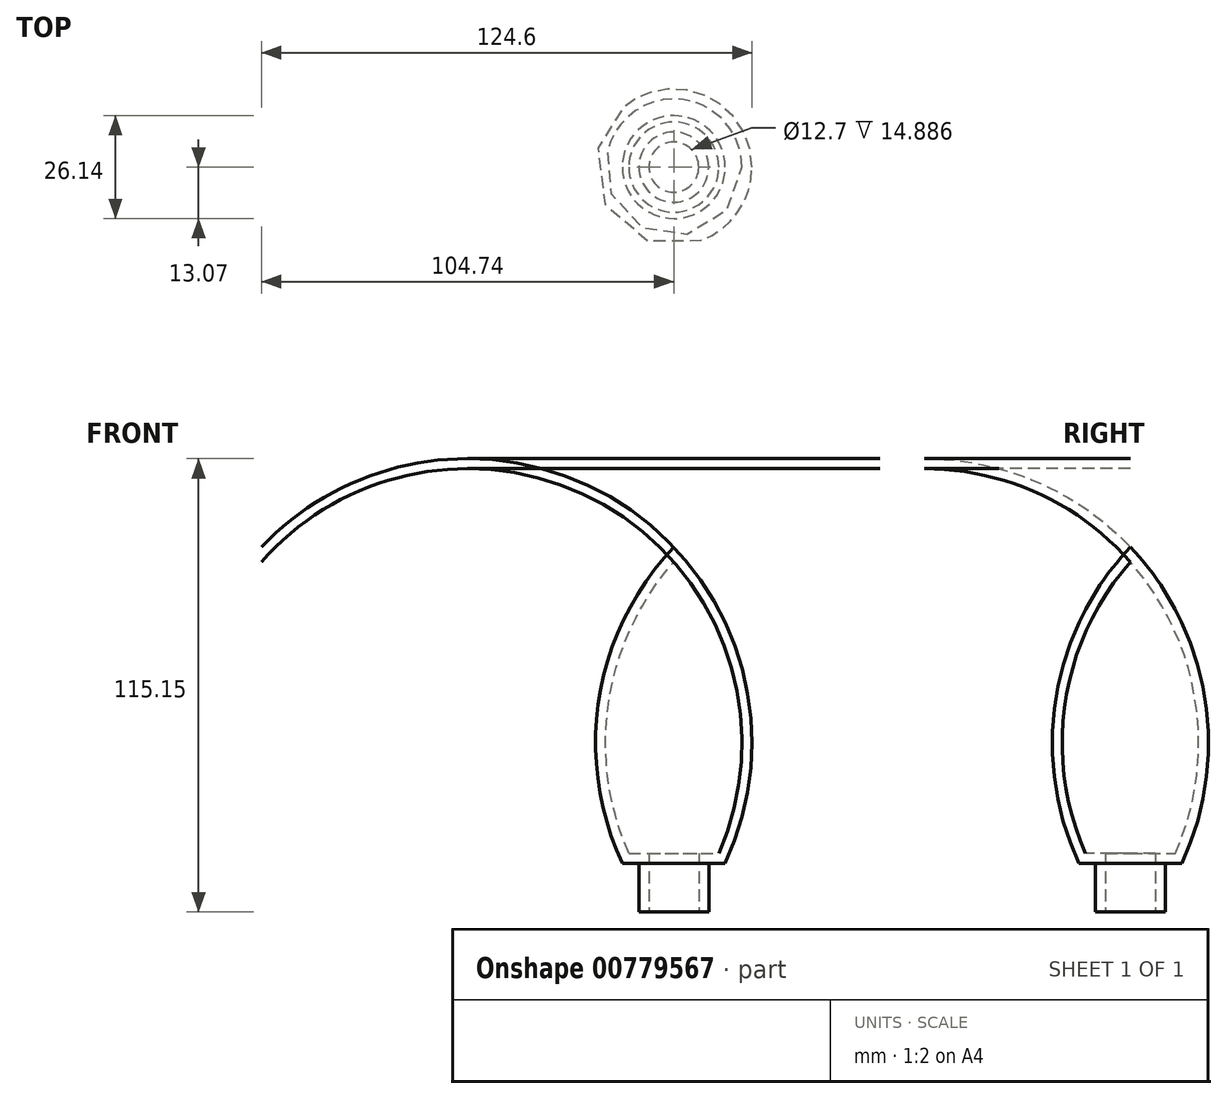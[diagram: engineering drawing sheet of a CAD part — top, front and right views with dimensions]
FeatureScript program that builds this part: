
annotation { "Feature Type Name" : "Feature", "Feature Type Description" : "" }
export const myFeature = defineFeature(function(context is Context, id is Id, definition is map)
    precondition{}
    {
        {
            var Q0;
            Q0=qCreatedBy(makeId("Front.planeOp"),FACE);
            var sketch = newSketch(context, id + "F0", { "sketchPlane" : qUnion([Q0])});
            skLineSegment(sketch, "E0", {"start": v(0, 0) * mm, "end": v(0, 88.9) * mm});
            skLineSegment(sketch, "E1", {"start": v(6.35, 0) * mm, "end": v(6.35, 14.89) * mm});
            skLineSegment(sketch, "E2", {"start": v(6.35, 14.89) * mm, "end": v(11.43, 14.89) * mm});
            skArc(sketch, "E3", {"start": v(11.43, 14.89) * mm, "mid": v(16.5, 53.56) * mm, "end": v(0, 88.9) * mm});
            skArc(sketch, "E4.0", {"start": v(13.07, 12.35) * mm, "mid": v(18.28, 57.96) * mm, "end": v(-5.05, 97.5) * mm});
            skLineSegment(sketch, "E4.1", {"start": v(8.9, 12.35) * mm, "end": v(13.07, 12.35) * mm});
            skLineSegment(sketch, "E4.2", {"start": v(8.9, 0) * mm, "end": v(8.9, 12.35) * mm});
            skLineSegment(sketch, "E5", {"start": v(6.35, 0) * mm, "end": v(8.9, 0) * mm});
            skLineSegment(sketch, "E6", {"start": v(0, 88.9) * mm, "end": v(0, 97.5) * mm});
            skLineSegment(sketch, "E7", {"start": v(0, 97.5) * mm, "end": v(0, 92.67) * mm});
            skSolve(sketch);
        }
        {
            var Q0;
            Q0=makeQuery(id+"F0.imprint","IMPRINT",FACE,{"disambiguationData":[TD([[makeQuery(id+"F0.imprint","IMPRINT",EDGE,{"derivedFrom":sQuery(id+"F0.wireOp",EDGE,"E1")}),-1.0]])]});
            var Q1;
            Q1=sQuery(id+"F0.wireOp",EDGE,"E0");
            revolve(context, id + "F1", {"surfaceOperationType" : NewSurfaceOperationType.NEW, "entities" : qUnion([Q0]), "axis" : qUnion([Q1]), "revolveType" : RevolveType.FULL});
        }
    });
